# Revit family: 306_7940a5b983504019abf719900e8a06
name_source: partatom
category: Pipe Accessories
units: mm (PartAtom-declared; Revit-internal decimal feet)

## family parameters
Always vertical = Yes
Cut with Voids When Loaded = No
Part Type = Valve - Breaks Into
Round Connector Dimension = Use Diameter
Shared = No
Work Plane-Based = No

## types (12) — shared parameters
CAT0 = Yes
Description = 2-way Control valve VLE122, PN16 external thread
L2D_Min = 3048 mm
Manufacturer = ESBE
QmdConnectorList = 301;D;302;D
URL = http://www.esbe.eu
Z4 = 13 mm
Z5 = 4 mm  [stored 0.0131234 ft]
Z6 = 2 mm  [stored 0.00656168 ft]
Z7 = 15 mm  [stored 0.0492126 ft]
magiPartTypeId = 306
magiProductFamilyId = 7940a5b983504019abf719900e8a06

## per-type parameters (varying)
- VLE122 PN16 G1 1/2 DN25-10: CenSd_D6_6=13 mm; D=25 mm; D1=29 mm; D13=13 mm; D2=24 mm; D3=21 mm; D4=19 mm; D5=20 mm  [stored 0.0656168 ft]; D6=15 mm  [stored 0.0492126 ft]; D7=11 mm; D8=5 mm  [stored 0.0164042 ft]; D9=5 mm  [stored 0.0164042 ft]; DN=20 mm  [stored 0.0656168 ft]; DN1=17 mm  [stored 0.0557743 ft]; DN2=15 mm  [stored 0.0492126 ft]; H3=39 mm  [stored 0.127953 ft]; H4=34 mm  [stored 0.111549 ft]; L2=78 mm; L2D=105 mm; LT2=53 mm; W2D=25 mm  [stored 0.082021 ft]; X1=3 mm  [stored 0.00984252 ft]; XN=11 mm; XN__ve=-11 mm; Z1=8 mm  [stored 0.0262467 ft]; Z11=9 mm  [stored 0.0295276 ft]; Z12=26 mm; Z2=51 mm; magiProductId=eae2e8fc1a0e4a5d97f1fc75064df0
- VLE122 PN16 G2 DN32-16: CenSd_D6_6=13 mm; D=32 mm; D1=29 mm; D13=13 mm; D2=24 mm; D3=21 mm; D4=19 mm; D5=20 mm  [stored 0.0656168 ft]; D6=15 mm  [stored 0.0492126 ft]; D7=11 mm; D8=5 mm  [stored 0.0164042 ft]; D9=5 mm  [stored 0.0164042 ft]; DN=25 mm  [stored 0.082021 ft]; DN1=21 mm; DN2=19 mm; H3=39 mm  [stored 0.127953 ft]; H4=35 mm; L2=78 mm; L2D=105 mm; LT2=53 mm; W2D=32 mm; X1=3 mm  [stored 0.00984252 ft]; XN=11 mm; XN__ve=-11 mm; Z1=8 mm  [stored 0.0262467 ft]; Z11=9 mm  [stored 0.0295276 ft]; Z12=26 mm; Z2=53 mm; magiProductId=3abf7c05b1e84195962e1b9c3be549
- VLE122 PN16 G2 3/4 DN50-38: CenSd_D6_6=19 mm; D=50 mm; D1=42 mm; D13=18 mm; D2=34 mm  [stored 0.111549 ft]; D3=30 mm  [stored 0.0984252 ft]; D4=27 mm; D5=29 mm; D6=22 mm; D7=15 mm  [stored 0.0492126 ft]; D8=8 mm  [stored 0.0262467 ft]; D9=7 mm  [stored 0.0229659 ft]; DN=35 mm; DN1=30 mm  [stored 0.0984252 ft]; DN2=26 mm; H3=58 mm; H4=53 mm; L2=111 mm; L2D=150 mm; LT2=75 mm; W2D=50 mm; X1=5 mm  [stored 0.0164042 ft]; XN=15 mm  [stored 0.0492126 ft]; XN__ve=-15 mm  [stored -0.0492126 ft]; Z1=12 mm  [stored 0.0393701 ft]; Z11=13 mm; Z12=40 mm; Z2=80 mm; magiProductId=bfb3d19f93354c9cadfca1234f33aa
- VLE122 PN16 G2 1/4 DN40-25: CenSd_D6_6=16 mm; D=40 mm; D1=36 mm; D13=16 mm; D2=29 mm; D3=26 mm; D4=24 mm; D5=25 mm  [stored 0.082021 ft]; D6=19 mm; D7=13 mm; D8=7 mm  [stored 0.0229659 ft]; D9=6 mm  [stored 0.019685 ft]; DN=30 mm  [stored 0.0984252 ft]; DN1=26 mm; DN2=23 mm; H3=48 mm; H4=42 mm; L2=96 mm; L2D=130 mm; LT2=65 mm; W2D=40 mm; X1=4 mm  [stored 0.0131234 ft]; XN=13 mm; XN__ve=-13 mm; Z1=10 mm  [stored 0.0328084 ft]; Z11=11 mm; Z12=32 mm; Z2=63 mm; magiProductId=a03c6edc50ee4670a6d3186b66dc3a
- VLE122 PN16 G1 DN15-4,0: CenSd_D6_6=12 mm  [stored 0.0393701 ft]; D=15 mm; D1=28 mm; D13=12 mm  [stored 0.0393701 ft]; D2=22 mm; D3=20 mm  [stored 0.0656168 ft]; D4=18 mm; D5=19 mm; D6=14 mm  [stored 0.0459318 ft]; D7=10 mm  [stored 0.0328084 ft]; D8=5 mm  [stored 0.0164042 ft]; D9=5 mm  [stored 0.0164042 ft]; DN=13 mm; DN1=11 mm; DN2=9 mm  [stored 0.0295276 ft]; H3=36 mm; H4=24 mm; L2=74 mm; L2D=100 mm; LT2=50 mm; W2D=15 mm  [stored 0.0492126 ft]; X1=3 mm  [stored 0.00984252 ft]; XN=10 mm  [stored 0.0328084 ft]; XN__ve=-10 mm  [stored -0.0328084 ft]; Z1=7 mm  [stored 0.0229659 ft]; Z11=6 mm  [stored 0.019685 ft]; Z12=18 mm; Z2=36 mm; magiProductId=fea057d96d95416b90287e93636704
- VLE122 PN16 G1 DN15-2,5: CenSd_D6_6=12 mm  [stored 0.0393701 ft]; D=15 mm; D1=28 mm; D13=12 mm  [stored 0.0393701 ft]; D2=22 mm; D3=20 mm  [stored 0.0656168 ft]; D4=18 mm; D5=19 mm; D6=14 mm  [stored 0.0459318 ft]; D7=10 mm  [stored 0.0328084 ft]; D8=5 mm  [stored 0.0164042 ft]; D9=5 mm  [stored 0.0164042 ft]; DN=13 mm; DN1=11 mm; DN2=9 mm  [stored 0.0295276 ft]; H3=36 mm; H4=24 mm; L2=74 mm; L2D=100 mm; LT2=50 mm; W2D=15 mm  [stored 0.0492126 ft]; X1=3 mm  [stored 0.00984252 ft]; XN=10 mm  [stored 0.0328084 ft]; XN__ve=-10 mm  [stored -0.0328084 ft]; Z1=7 mm  [stored 0.0229659 ft]; Z11=6 mm  [stored 0.019685 ft]; Z12=18 mm; Z2=36 mm; magiProductId=b87672ecabe64393a94d029542a7de
- VLE122 PN16 G1 DN15-1,6: CenSd_D6_6=12 mm  [stored 0.0393701 ft]; D=15 mm; D1=28 mm; D13=12 mm  [stored 0.0393701 ft]; D2=22 mm; D3=20 mm  [stored 0.0656168 ft]; D4=18 mm; D5=19 mm; D6=14 mm  [stored 0.0459318 ft]; D7=10 mm  [stored 0.0328084 ft]; D8=5 mm  [stored 0.0164042 ft]; D9=5 mm  [stored 0.0164042 ft]; DN=13 mm; DN1=11 mm; DN2=9 mm  [stored 0.0295276 ft]; H3=36 mm; H4=24 mm; L2=74 mm; L2D=100 mm; LT2=50 mm; W2D=15 mm  [stored 0.0492126 ft]; X1=3 mm  [stored 0.00984252 ft]; XN=10 mm  [stored 0.0328084 ft]; XN__ve=-10 mm  [stored -0.0328084 ft]; Z1=7 mm  [stored 0.0229659 ft]; Z11=6 mm  [stored 0.019685 ft]; Z12=18 mm; Z2=36 mm; magiProductId=493f53e1b07d4fa7b52e1f5343ce7d
- VLE122 PN16 G1 DN15-1,0: CenSd_D6_6=12 mm  [stored 0.0393701 ft]; D=15 mm; D1=28 mm; D13=12 mm  [stored 0.0393701 ft]; D2=22 mm; D3=20 mm  [stored 0.0656168 ft]; D4=18 mm; D5=19 mm; D6=14 mm  [stored 0.0459318 ft]; D7=10 mm  [stored 0.0328084 ft]; D8=5 mm  [stored 0.0164042 ft]; D9=5 mm  [stored 0.0164042 ft]; DN=13 mm; DN1=11 mm; DN2=9 mm  [stored 0.0295276 ft]; H3=36 mm; H4=24 mm; L2=74 mm; L2D=100 mm; LT2=50 mm; W2D=15 mm  [stored 0.0492126 ft]; X1=3 mm  [stored 0.00984252 ft]; XN=10 mm  [stored 0.0328084 ft]; XN__ve=-10 mm  [stored -0.0328084 ft]; Z1=7 mm  [stored 0.0229659 ft]; Z11=6 mm  [stored 0.019685 ft]; Z12=18 mm; Z2=36 mm; magiProductId=3f289e3e0d224b81b59ec61cb125f9
- VLE122 PN16 G1 DN15-0,63: CenSd_D6_6=12 mm  [stored 0.0393701 ft]; D=15 mm; D1=28 mm; D13=12 mm  [stored 0.0393701 ft]; D2=22 mm; D3=20 mm  [stored 0.0656168 ft]; D4=18 mm; D5=19 mm; D6=14 mm  [stored 0.0459318 ft]; D7=10 mm  [stored 0.0328084 ft]; D8=5 mm  [stored 0.0164042 ft]; D9=5 mm  [stored 0.0164042 ft]; DN=13 mm; DN1=11 mm; DN2=9 mm  [stored 0.0295276 ft]; H3=36 mm; H4=24 mm; L2=74 mm; L2D=100 mm; LT2=50 mm; W2D=15 mm  [stored 0.0492126 ft]; X1=3 mm  [stored 0.00984252 ft]; XN=10 mm  [stored 0.0328084 ft]; XN__ve=-10 mm  [stored -0.0328084 ft]; Z1=7 mm  [stored 0.0229659 ft]; Z11=6 mm  [stored 0.019685 ft]; Z12=18 mm; Z2=36 mm; magiProductId=45e5c653b7134c6691d36cd144b5f2
- VLE122 PN16 G1 DN15-0,4: CenSd_D6_6=12 mm  [stored 0.0393701 ft]; D=15 mm; D1=28 mm; D13=12 mm  [stored 0.0393701 ft]; D2=22 mm; D3=20 mm  [stored 0.0656168 ft]; D4=18 mm; D5=19 mm; D6=14 mm  [stored 0.0459318 ft]; D7=10 mm  [stored 0.0328084 ft]; D8=5 mm  [stored 0.0164042 ft]; D9=5 mm  [stored 0.0164042 ft]; DN=13 mm; DN1=11 mm; DN2=9 mm  [stored 0.0295276 ft]; H3=36 mm; H4=24 mm; L2=74 mm; L2D=100 mm; LT2=50 mm; W2D=15 mm  [stored 0.0492126 ft]; X1=3 mm  [stored 0.00984252 ft]; XN=10 mm  [stored 0.0328084 ft]; XN__ve=-10 mm  [stored -0.0328084 ft]; Z1=7 mm  [stored 0.0229659 ft]; Z11=6 mm  [stored 0.019685 ft]; Z12=18 mm; Z2=36 mm; magiProductId=793a6328c7854b8083969c4476e7bd
- VLE122 PN16 G1 DN15-0,25: CenSd_D6_6=12 mm  [stored 0.0393701 ft]; D=15 mm; D1=28 mm; D13=12 mm  [stored 0.0393701 ft]; D2=22 mm; D3=20 mm  [stored 0.0656168 ft]; D4=18 mm; D5=19 mm; D6=14 mm  [stored 0.0459318 ft]; D7=10 mm  [stored 0.0328084 ft]; D8=5 mm  [stored 0.0164042 ft]; D9=5 mm  [stored 0.0164042 ft]; DN=13 mm; DN1=11 mm; DN2=9 mm  [stored 0.0295276 ft]; H3=36 mm; H4=24 mm; L2=74 mm; L2D=100 mm; LT2=50 mm; W2D=15 mm  [stored 0.0492126 ft]; X1=3 mm  [stored 0.00984252 ft]; XN=10 mm  [stored 0.0328084 ft]; XN__ve=-10 mm  [stored -0.0328084 ft]; Z1=7 mm  [stored 0.0229659 ft]; Z11=6 mm  [stored 0.019685 ft]; Z12=18 mm; Z2=36 mm; magiProductId=d5913ecdc0e048b89ebc240f88ceb5
- VLE122 PN16 G1 1/4 DN20-6,3: CenSd_D6_6=12 mm  [stored 0.0393701 ft]; D=20 mm; D1=28 mm; D13=12 mm  [stored 0.0393701 ft]; D2=22 mm; D3=20 mm  [stored 0.0656168 ft]; D4=18 mm; D5=19 mm; D6=14 mm  [stored 0.0459318 ft]; D7=10 mm  [stored 0.0328084 ft]; D8=5 mm  [stored 0.0164042 ft]; D9=5 mm  [stored 0.0164042 ft]; DN=16 mm; DN1=14 mm  [stored 0.0459318 ft]; DN2=12 mm  [stored 0.0393701 ft]; H3=38 mm; H4=30 mm  [stored 0.0984252 ft]; L2=74 mm; L2D=100 mm; LT2=50 mm; W2D=20 mm  [stored 0.0656168 ft]; X1=3 mm  [stored 0.00984252 ft]; XN=10 mm  [stored 0.0328084 ft]; XN__ve=-10 mm  [stored -0.0328084 ft]; Z1=8 mm  [stored 0.0262467 ft]; Z11=8 mm  [stored 0.0262467 ft]; Z12=23 mm; Z2=45 mm; magiProductId=76cfcf91c56f4ec08b0bcf0ceb75ad

note: column(s) folded — value = type name in every type: magiProductCode

note: [stored X ft] marks values corroborated as IEEE doubles in the binary element streams (Revit-internal decimal feet)

## geometry (parser evidence)
native form markers: Sweep x2
no freeform markers — native parametric forms only
